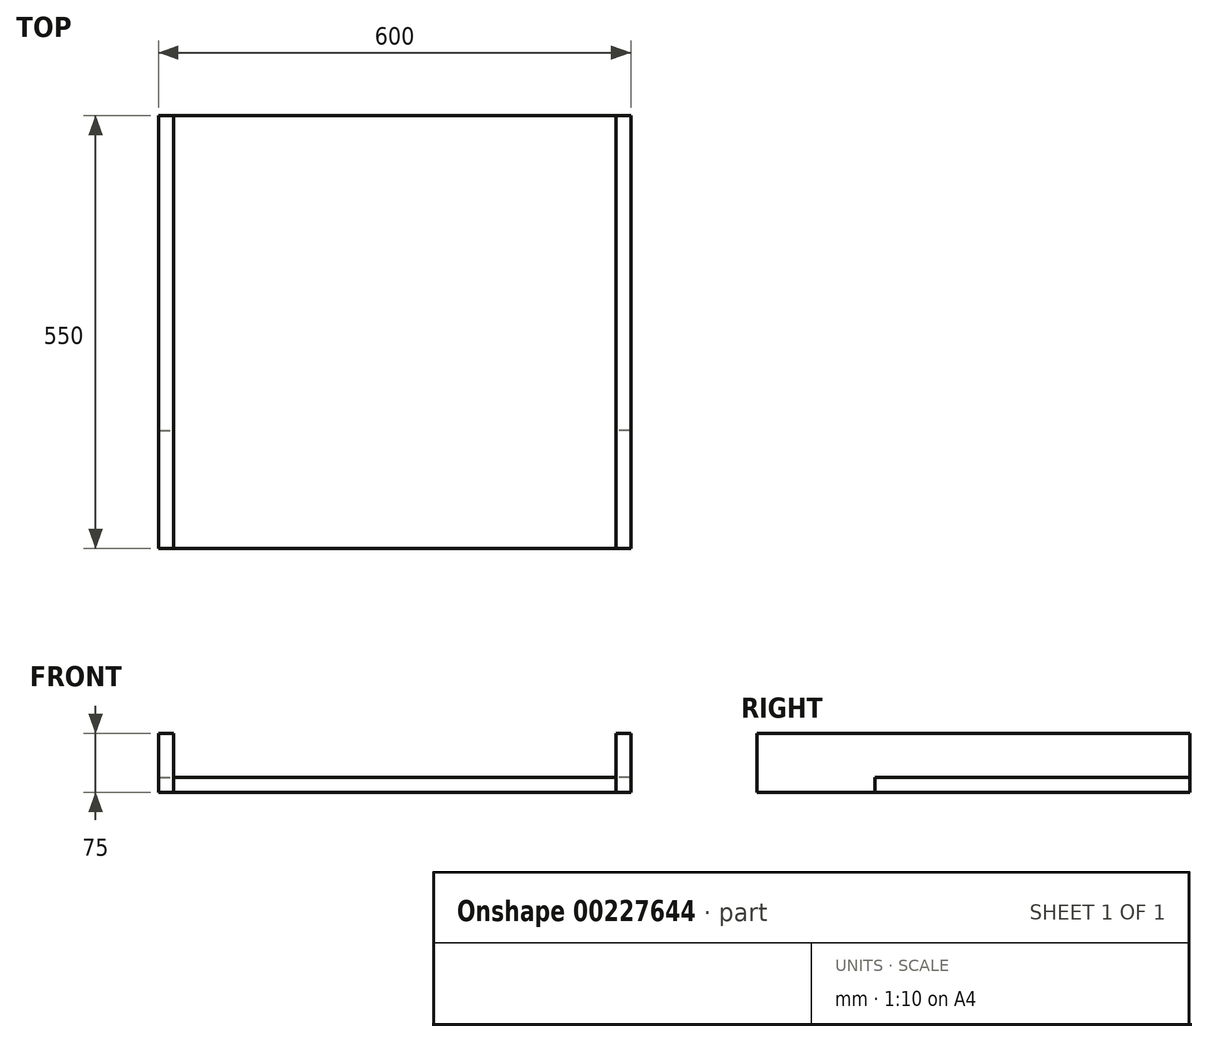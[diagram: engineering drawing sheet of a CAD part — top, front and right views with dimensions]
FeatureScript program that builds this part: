
annotation { "Feature Type Name" : "Feature", "Feature Type Description" : "" }
export const myFeature = defineFeature(function(context is Context, id is Id, definition is map)
    precondition{}
    {
        {
            var Q0;
            Q0=qCreatedBy(makeId("Front.planeOp"),FACE);
            var sketch = newSketch(context, id + "F0", { "sketchPlane" : qUnion([Q0])});
            skLineSegment(sketch, "E0.bottom", {"start": v(23.9, 75) * mm, "end": v(573.9, 75) * mm});
            skLineSegment(sketch, "E0.top", {"start": v(23.9, 0) * mm, "end": v(573.9, 0) * mm});
            skLineSegment(sketch, "E0.left", {"start": v(23.9, 75) * mm, "end": v(23.9, 0) * mm});
            skLineSegment(sketch, "E0.right", {"start": v(573.9, 75) * mm, "end": v(573.9, 0) * mm});
            skLineSegment(sketch, "E1.bottom", {"start": v(23.9, 0) * mm, "end": v(423.9, 0) * mm});
            skLineSegment(sketch, "E1.top", {"start": v(23.9, 19) * mm, "end": v(423.9, 19) * mm});
            skLineSegment(sketch, "E1.left", {"start": v(23.9, 0) * mm, "end": v(23.9, 19) * mm});
            skLineSegment(sketch, "E1.right", {"start": v(423.9, 0) * mm, "end": v(423.9, 19) * mm});
            skSolve(sketch);
        }
        {
            var Q0;
            Q0=qCreatedBy(makeId("Top.planeOp"),FACE);
            var sketch = newSketch(context, id + "F1", { "sketchPlane" : qUnion([Q0])});
            skLineSegment(sketch, "E2.bottom", {"start": v(23.9, 0) * mm, "end": v(573.9, 0) * mm});
            skLineSegment(sketch, "E2.top", {"start": v(23.9, 562) * mm, "end": v(573.9, 562) * mm});
            skLineSegment(sketch, "E2.left", {"start": v(23.9, 0) * mm, "end": v(23.9, 562) * mm});
            skLineSegment(sketch, "E2.right", {"start": v(573.9, 0) * mm, "end": v(573.9, 562) * mm});
            skLineSegment(sketch, "E3.bottom", {"start": v(23.9, 0) * mm, "end": v(63.68, 0) * mm});
            skLineSegment(sketch, "E3.top", {"start": v(23.9, -19) * mm, "end": v(63.68, -19) * mm});
            skLineSegment(sketch, "E3.left", {"start": v(23.9, 0) * mm, "end": v(23.9, -19) * mm});
            skLineSegment(sketch, "E3.right", {"start": v(63.68, 0) * mm, "end": v(63.68, -19) * mm});
            skLineSegment(sketch, "E4.bottom", {"start": v(23.9, 562) * mm, "end": v(63.68, 562) * mm});
            skLineSegment(sketch, "E4.top", {"start": v(23.9, 581) * mm, "end": v(63.68, 581) * mm});
            skLineSegment(sketch, "E4.left", {"start": v(23.9, 562) * mm, "end": v(23.9, 581) * mm});
            skLineSegment(sketch, "E4.right", {"start": v(63.68, 562) * mm, "end": v(63.68, 581) * mm});
            skSolve(sketch);
        }
        {
            var Q0;
            Q0=makeQuery(id+"F0.imprint","IMPRINT",FACE,{"disambiguationData":[TD([[makeQuery(id+"F0.imprint","IMPRINT",EDGE,{"derivedFrom":sQuery(id+"F0.wireOp",EDGE,"E0.bottom")}),-1.0]])]});
            var Q1;
            Q1=sQuery(id+"F1.wireOp",VERTEX,"E3.top.end");
            extrude(context, id + "F2", {"entities" : qUnion([Q0]), "endBound" : BoundingType.UP_TO_VERTEX, "endBoundEntityVertex" : qUnion([Q1]), "depth" : 25 * mm});
        }
        {
            var Q0;
            Q0=makeQuery(id+"F0.imprint","IMPRINT",FACE,{"disambiguationData":[TD([[makeQuery(id+"F0.imprint","IMPRINT",EDGE,{"derivedFrom":sQuery(id+"F0.wireOp",EDGE,"E0.bottom")}),-1.0]])]});
            var Q1;
            Q1=sQuery(id+"F1.wireOp",VERTEX,"E4.top.end");
            var Q2;
            Q2=sQuery(id+"F1.wireOp",VERTEX,"E2.left.end");
            extrude(context, id + "F3", {"entities" : qUnion([Q0]), "endBound" : BoundingType.UP_TO_VERTEX, "oppositeDirection" : true, "endBoundEntityVertex" : qUnion([Q1]), "depth" : 25 * mm, "hasSecondDirection" : true, "secondDirectionBound" : BoundingType.UP_TO_VERTEX, "secondDirectionOppositeDirection" : true, "secondDirectionBoundEntityVertex" : qUnion([Q2]), "secondDirectionDepth" : 25 * mm});
        }
        {
            var Q0;
            Q0=makeQuery(id+"F1.imprint","IMPRINT",FACE,{"disambiguationData":[TD([[makeQuery(id+"F1.imprint","IMPRINT",EDGE,{"derivedFrom":sQuery(id+"F1.wireOp",EDGE,"E2.bottom")}),1.0]])]});
            var Q1;
            Q1=makeQuery(id+"F1.imprint","IMPRINT",FACE,{"disambiguationData":[TD([[makeQuery(id+"F1.imprint","IMPRINT",EDGE,{"derivedFrom":sQuery(id+"F1.wireOp",EDGE,"E3.bottom")}),-1.0]])]});
            var Q2;
            Q2=makeQuery(id+"F1.imprint","IMPRINT",FACE,{"disambiguationData":[TD([[makeQuery(id+"F1.imprint","IMPRINT",EDGE,{"derivedFrom":sQuery(id+"F1.wireOp",EDGE,"E4.bottom")}),1.0]])]});
            var Q3;
            Q3=sQuery(id+"F0.wireOp",VERTEX,"E1.top.start");
            extrude(context, id + "F4", {"entities" : qUnion([Q0, Q1, Q2]), "endBound" : BoundingType.UP_TO_VERTEX, "endBoundEntityVertex" : qUnion([Q3]), "depth" : 25 * mm});
        }
        {
            var Q0;
            Q0=makeQuery(id+"F3.opExtrude","SWEPT_BODY",BODY,{"disambiguationData":[OSD([sQuery(id+"F0.wireOp",EDGE,"E0.bottom"),sQuery(id+"F0.wireOp",EDGE,"E0.top"),sQuery(id+"F0.wireOp",EDGE,"E0.left"),sQuery(id+"F0.wireOp",EDGE,"E0.right"),sQuery(id+"F0.wireOp",EDGE,"E1.top"),sQuery(id+"F0.wireOp",EDGE,"E1.right")])]});
            var Q1;
            Q1=makeQuery(id+"F4.opExtrude","SWEPT_BODY",BODY,{"disambiguationData":[OSD([sQuery(id+"F1.wireOp",EDGE,"E2.bottom"),sQuery(id+"F1.wireOp",EDGE,"E2.top"),sQuery(id+"F1.wireOp",EDGE,"E2.left"),sQuery(id+"F1.wireOp",EDGE,"E2.right"),sQuery(id+"F1.wireOp",EDGE,"E3.top"),sQuery(id+"F1.wireOp",EDGE,"E3.left"),sQuery(id+"F1.wireOp",EDGE,"E3.right"),sQuery(id+"F1.wireOp",EDGE,"E4.top"),sQuery(id+"F1.wireOp",EDGE,"E4.left"),sQuery(id+"F1.wireOp",EDGE,"E4.right")])]});
            var Q2;
            Q2=makeQuery(id+"F2.opExtrude","SWEPT_BODY",BODY,{"disambiguationData":[OSD([sQuery(id+"F0.wireOp",EDGE,"E0.bottom"),sQuery(id+"F0.wireOp",EDGE,"E0.top"),sQuery(id+"F0.wireOp",EDGE,"E0.left"),sQuery(id+"F0.wireOp",EDGE,"E0.right"),sQuery(id+"F0.wireOp",EDGE,"E1.top"),sQuery(id+"F0.wireOp",EDGE,"E1.right")])]});
            var Q3;
            Q3=sQuery(id+"F0.wireOp",EDGE,"E0.left");
            transform(context, id + "F5", {"entities" : qUnion([Q0, Q1, Q2]), "transformType" : TransformType.ROTATION, "transformAxis" : qUnion([Q3]), "angle" : 90 * degree, "makeCopy" : false});
        }
    });
